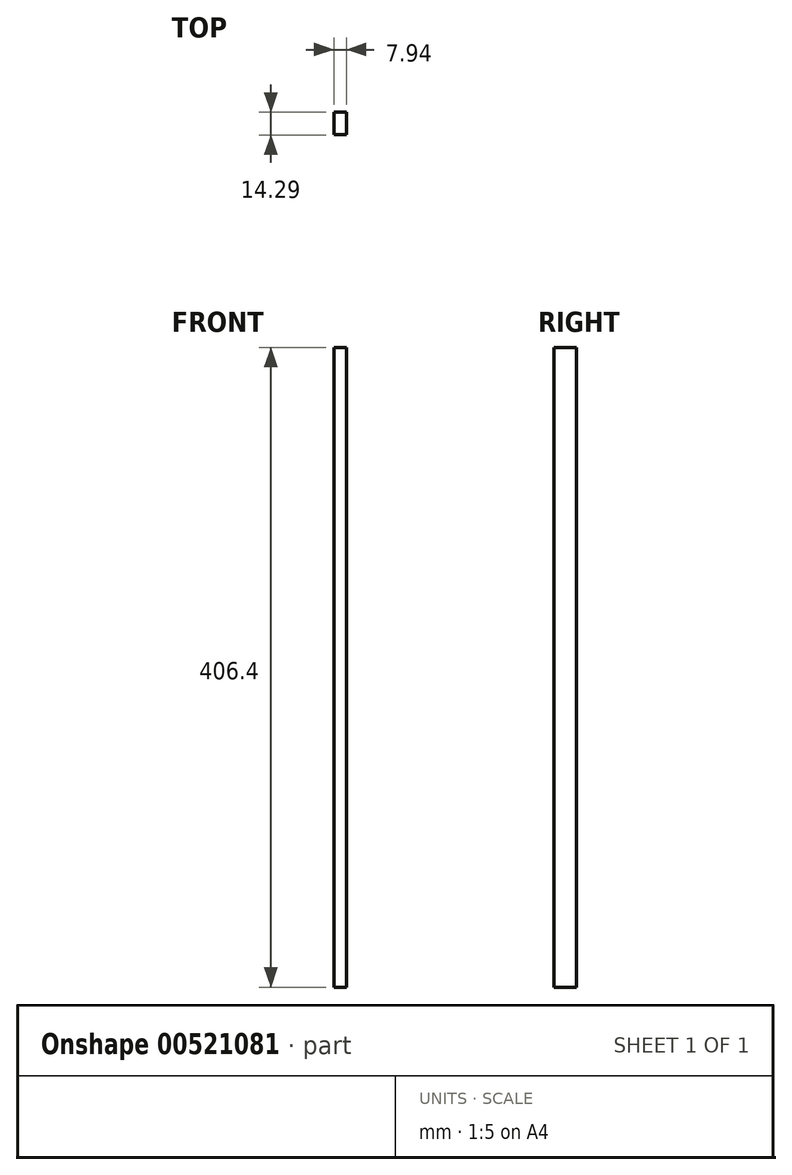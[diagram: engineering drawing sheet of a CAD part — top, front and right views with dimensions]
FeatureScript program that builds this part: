
annotation { "Feature Type Name" : "Feature", "Feature Type Description" : "" }
export const myFeature = defineFeature(function(context is Context, id is Id, definition is map)
    precondition{}
    {
        {
            var Q0;
            Q0=qCreatedBy(makeId("Top.planeOp"),FACE);
            var sketch = newSketch(context, id + "F0", { "sketchPlane" : qUnion([Q0])});
            skLineSegment(sketch, "E0", {"start": v(0, 84.2) * mm, "end": v(0, -97.88) * mm, "construction": true});
            skLineSegment(sketch, "E1", {"start": v(-103.43, 0) * mm, "end": v(103, 0) * mm, "construction": true});
            skLineSegment(sketch, "E2.bottom", {"start": v(-22.22, 57.15) * mm, "end": v(22.22, 57.15) * mm});
            skLineSegment(sketch, "E2.top", {"start": v(-22.22, -57.15) * mm, "end": v(22.23, -57.15) * mm});
            skLineSegment(sketch, "E2.left", {"start": v(-22.22, 57.15) * mm, "end": v(-22.22, -57.15) * mm});
            skLineSegment(sketch, "E2.right", {"start": v(22.23, 57.15) * mm, "end": v(22.23, -57.15) * mm});
            skLineSegment(sketch, "E3", {"start": v(14.29, 57.15) * mm, "end": v(14.29, -57.15) * mm, "construction": true});
            skLineSegment(sketch, "E4.bottom", {"start": v(22.22, 57.15) * mm, "end": v(14.29, 57.15) * mm});
            skLineSegment(sketch, "E4.top", {"start": v(22.23, 42.86) * mm, "end": v(14.29, 42.86) * mm});
            skLineSegment(sketch, "E4.left", {"start": v(22.22, 57.15) * mm, "end": v(22.22, 42.86) * mm});
            skLineSegment(sketch, "E4.right", {"start": v(14.29, 57.15) * mm, "end": v(14.29, 42.86) * mm});
            skLineSegment(sketch, "E5.0.1.0", {"start": v(22.23, 14.29) * mm, "end": v(14.29, 14.29) * mm});
            skLineSegment(sketch, "E5.0.1.1", {"start": v(14.29, 28.58) * mm, "end": v(14.29, 14.29) * mm});
            skLineSegment(sketch, "E5.0.1.2", {"start": v(22.22, 28.58) * mm, "end": v(14.29, 28.58) * mm});
            skLineSegment(sketch, "E5.0.2.0", {"start": v(22.23, -14.29) * mm, "end": v(14.29, -14.29) * mm});
            skLineSegment(sketch, "E5.0.2.1", {"start": v(14.29, 0) * mm, "end": v(14.29, -14.29) * mm});
            skLineSegment(sketch, "E5.0.2.2", {"start": v(22.22, 0) * mm, "end": v(14.29, 0) * mm});
            skLineSegment(sketch, "E5.0.3.0", {"start": v(22.23, -42.86) * mm, "end": v(14.29, -42.86) * mm});
            skLineSegment(sketch, "E5.0.3.1", {"start": v(14.29, -28.58) * mm, "end": v(14.29, -42.86) * mm});
            skLineSegment(sketch, "E5.0.3.2", {"start": v(22.22, -28.58) * mm, "end": v(14.29, -28.58) * mm});
            skLineSegment(sketch, "E5.direction1", {"start": v(14.29, 42.86) * mm, "end": v(39.69, 42.86) * mm, "construction": true});
            skLineSegment(sketch, "E5.direction2", {"start": v(14.29, 42.86) * mm, "end": v(14.29, 14.29) * mm, "construction": true});
            skSolve(sketch);
        }
        {
            var Q0;
            Q0=makeQuery(id+"F0.imprint","IMPRINT",FACE,{"disambiguationData":[TD([[makeQuery(id+"F0.imprint","IMPRINT",EDGE,{"derivedFrom":sQuery(id+"F0.wireOp",EDGE,"E2.bottom")}),-1.0]])]});
            extrude(context, id + "F1", {"entities" : qUnion([Q0]), "endBound" : BoundingType.SYMMETRIC, "depth" : 406.4 * mm, "offsetDistance" : 25.4 * mm});
        }
    });
